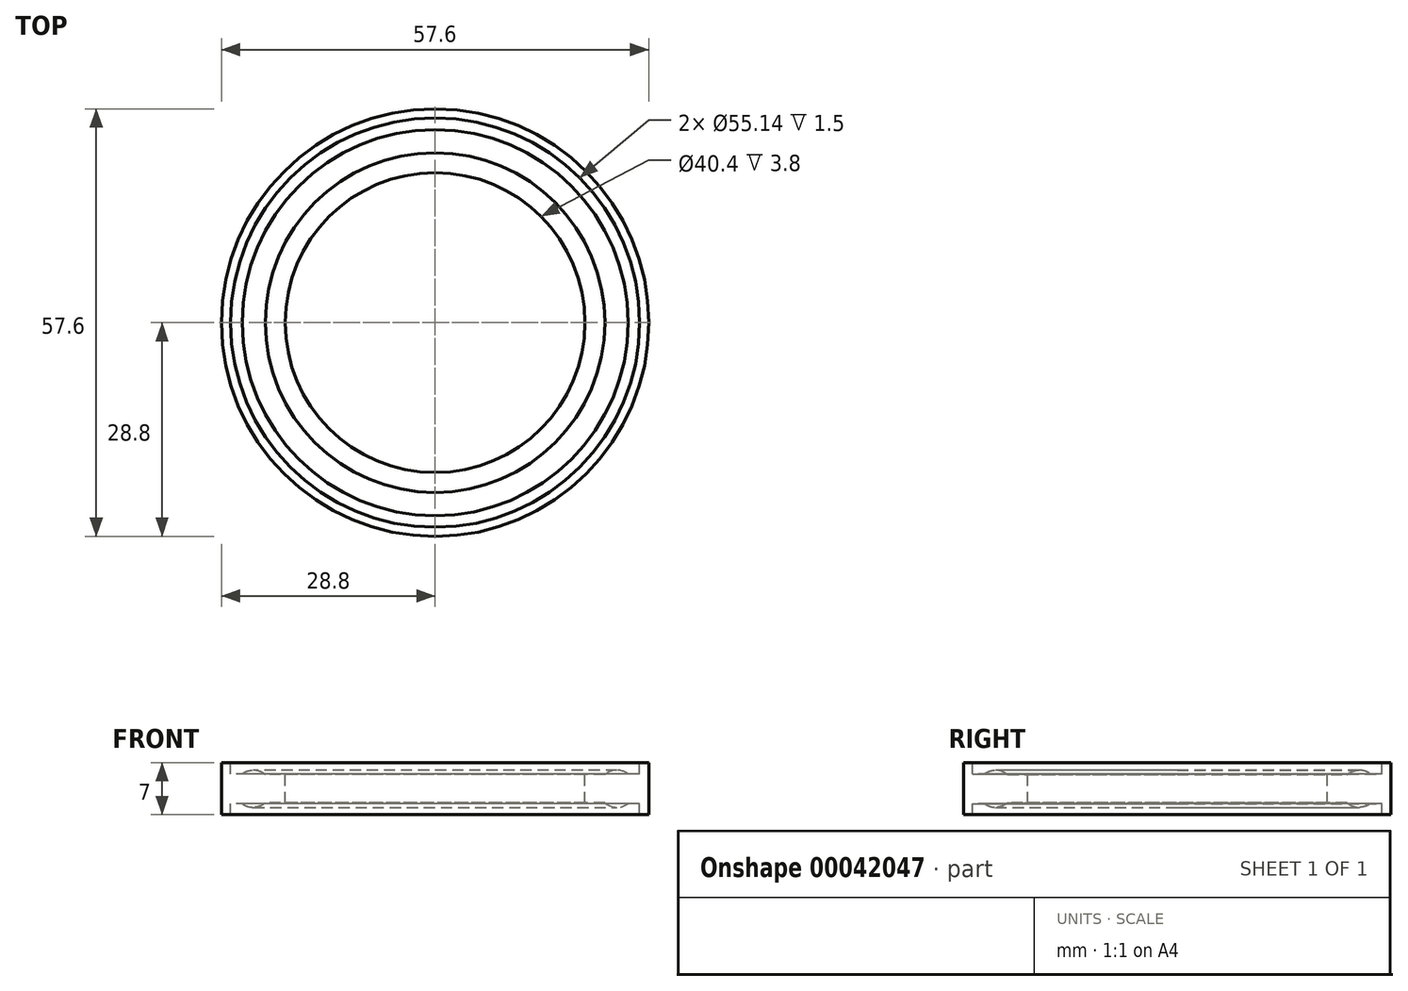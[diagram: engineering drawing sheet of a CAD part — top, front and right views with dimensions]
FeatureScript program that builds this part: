
annotation { "Feature Type Name" : "Feature", "Feature Type Description" : "" }
export const myFeature = defineFeature(function(context is Context, id is Id, definition is map)
    precondition{}
    {
        {
            var Q0;
            Q0=qCreatedBy(makeId("Front.planeOp"),FACE);
            var sketch = newSketch(context, id + "F0", { "sketchPlane" : qUnion([Q0])});
            skLineSegment(sketch, "E0", {"start": v(0, 7) * mm, "end": v(0, 0) * mm, "construction": true});
            skLineSegment(sketch, "E1", {"start": v(28.8, 7) * mm, "end": v(28.8, 0) * mm});
            skLineSegment(sketch, "E2", {"start": v(28.8, 7) * mm, "end": v(27.57, 7) * mm});
            skLineSegment(sketch, "E3", {"start": v(27.57, 7) * mm, "end": v(27.57, 5.5) * mm});
            skLineSegment(sketch, "E4", {"start": v(27.57, 5.5) * mm, "end": v(26.01, 5.5) * mm});
            skLineSegment(sketch, "E5", {"start": v(26.01, 1.5) * mm, "end": v(27.57, 1.5) * mm});
            skLineSegment(sketch, "E6", {"start": v(27.57, 1.5) * mm, "end": v(27.57, 0) * mm});
            skLineSegment(sketch, "E7", {"start": v(27.57, 0) * mm, "end": v(28.8, 0) * mm});
            skArc(sketch, "E8", {"start": v(26.01, 1.5) * mm, "mid": v(27.01, 3.5) * mm, "end": v(26.01, 5.5) * mm});
            skCircle(sketch, "E9", {"center": v(24.51, 3.5) * mm, "radius": 2.5 * mm});
            skLineSegment(sketch, "E10", {"start": v(24.51, 3.5) * mm, "end": v(18.55, 3.5) * mm, "construction": true});
            skLineSegment(sketch, "E11", {"start": v(22.89, 5.4) * mm, "end": v(20.2, 5.4) * mm});
            skLineSegment(sketch, "E12", {"start": v(20.2, 5.4) * mm, "end": v(20.2, 1.6) * mm});
            skLineSegment(sketch, "E13", {"start": v(20.2, 1.6) * mm, "end": v(22.89, 1.6) * mm});
            skSolve(sketch);
        }
        {
            var Q0;
            {var subQ1=sQuery(id+"F0.wireOp",EDGE,"E11");Q0=makeQuery(id+"F0.imprint","IMPRINT",FACE,{"disambiguationData":[TD([[makeQuery(id+"F0.imprint","IMPRINT",EDGE,{"derivedFrom":subQ1}),1.0]])]});}
            var Q1;
            {var subQ0=sQuery(id+"F0.wireOp",EDGE,"E9");var subQ2=makeQuery(id+"F0.imprint","INTERSECT",VERTEX,{"derivedFrom":[sQuery(id+"F0.wireOp",EDGE,"E4"),subQ0]});Q1=makeQuery(id+"F0.imprint","IMPRINT",FACE,{"disambiguationData":[TD([[makeQuery(id+"F0.imprint","IMPRINT",EDGE,{"disambiguationData":[TD([[subQ2,-1.0]])],"derivedFrom":subQ0}),1.0]])]});}
            var Q2;
            Q2=makeQuery(id+"F0.imprint","IMPRINT",FACE,{"disambiguationData":[TD([[makeQuery(id+"F0.imprint","IMPRINT",EDGE,{"derivedFrom":sQuery(id+"F0.wireOp",EDGE,"E1")}),-1.0]])]});
            var Q3;
            Q3=sQuery(id+"F0.wireOp",EDGE,"E0");
            revolve(context, id + "F1", {"entities" : qUnion([Q0, Q1, Q2]), "axis" : qUnion([Q3]), "revolveType" : RevolveType.FULL});
        }
    });
